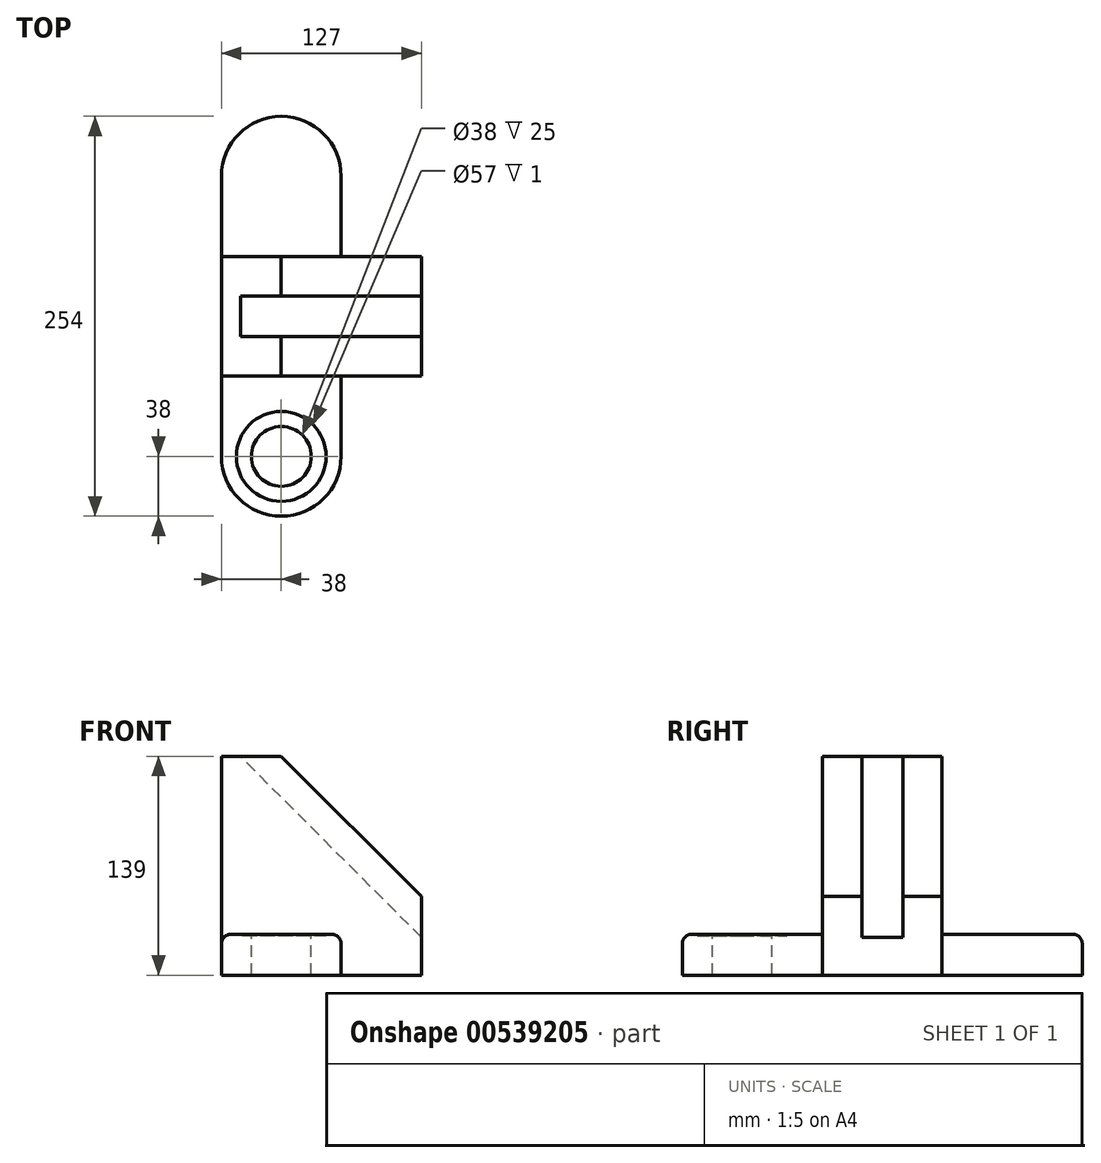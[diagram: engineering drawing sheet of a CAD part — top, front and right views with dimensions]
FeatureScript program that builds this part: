
annotation { "Feature Type Name" : "Feature", "Feature Type Description" : "" }
export const myFeature = defineFeature(function(context is Context, id is Id, definition is map)
    precondition{}
    {
        {
            assignVariable(context, id + "F0", {"name" : "b", "anyValue" : 38});
        }
        {
            var Q0;
            Q0=qCreatedBy(makeId("Top.planeOp"),FACE);
            var sketch = newSketch(context, id + "F1", { "sketchPlane" : qUnion([Q0])});
            skLineSegment(sketch, "E0.bottom", {"start": v(0, 0) * mm, "end": v(127, 0) * mm});
            skLineSegment(sketch, "E0.top", {"start": v(0, -76) * mm, "end": v(127, -76) * mm});
            skLineSegment(sketch, "E0.left", {"start": v(0, 0) * mm, "end": v(0, -76) * mm});
            skLineSegment(sketch, "E0.right", {"start": v(127, 0) * mm, "end": v(127, -76) * mm});
            skSolve(sketch);
        }
        {
            var Q0;
            Q0 = qSketchRegion(id + "F1", true);
            extrude(context, id + "F2", {"entities" : qUnion([Q0]), "depth" : (127 - getVariable(context, 'b') + 50) * mm, "offsetDistance" : 25 * mm});
        }
        {
            var Q0;
            Q0=makeQuery(id+"F2.opExtrude","CAP_FACE",FACE,{"disambiguationData":[OSD([sQuery(id+"F1.wireOp",EDGE,"E0.bottom"),sQuery(id+"F1.wireOp",EDGE,"E0.top"),sQuery(id+"F1.wireOp",EDGE,"E0.left"),sQuery(id+"F1.wireOp",EDGE,"E0.right")])],"isStart":true});
            var sketch = newSketch(context, id + "F3", { "sketchPlane" : qUnion([Q0])});
            skLineSegment(sketch, "E1", {"start": v(0, 127) * mm, "end": v(0, -51) * mm});
            skLineSegment(sketch, "E2", {"start": v(76, 127) * mm, "end": v(76, -51) * mm});
            skArc(sketch, "E3", {"start": v(0, 127) * mm, "mid": v(38, 165) * mm, "end": v(76, 127) * mm});
            skArc(sketch, "E4", {"start": v(0, -51) * mm, "mid": v(38, -89) * mm, "end": v(76, -51) * mm});
            skSolve(sketch);
        }
        {
            var Q0;
            Q0 = qSketchRegion(id + "F3", true);
            extrude(context, id + "F4", {"entities" : qUnion([Q0]), "operationType" : NewBodyOperationType.ADD, "oppositeDirection" : true, "depth" : 26 * mm, "offsetDistance" : 25 * mm});
        }
        {
            var Q0;
            {var subQ0=sQuery(id+"F3.wireOp",EDGE,"E2");var subQ1=sQuery(id+"F3.wireOp",EDGE,"E1");var subQ2=sQuery(id+"F3.wireOp",EDGE,"E3");Q0=makeQuery(id+"F4.boolean.opBoolean","SPLIT",FACE,{"disambiguationData":[TD([makeQuery(id+"F2.opExtrude","SWEPT_FACE",FACE,{"disambiguationData":[OSD([sQuery(id+"F1.wireOp",EDGE,"E0.top")])]})])],"derivedFrom":makeQuery(id+"F4.opExtrude","CAP_FACE",FACE,{"disambiguationData":[OSD([subQ1,subQ0,subQ2,sQuery(id+"F3.wireOp",EDGE,"E4")])],"isStart":false})});}
            var sketch = newSketch(context, id + "F5", { "sketchPlane" : qUnion([Q0])});
            skCircle(sketch, "E5", {"center": v(38, -127) * mm, "radius": 19 * mm});
            skSolve(sketch);
        }
        {
            var Q0;
            Q0 = qSketchRegion(id + "F5", true);
            extrude(context, id + "F6", {"entities" : qUnion([Q0]), "operationType" : NewBodyOperationType.REMOVE, "endBound" : BoundingType.UP_TO_NEXT, "oppositeDirection" : true, "depth" : 25 * mm, "offsetDistance" : 25 * mm});
        }
        {
            var Q0;
            {var subQ0=sQuery(id+"F3.wireOp",EDGE,"E2");var subQ1=sQuery(id+"F3.wireOp",EDGE,"E1");var subQ2=sQuery(id+"F3.wireOp",EDGE,"E3");Q0=makeQuery(id+"F4.boolean.opBoolean","SPLIT",FACE,{"disambiguationData":[TD([makeQuery(id+"F2.opExtrude","SWEPT_FACE",FACE,{"disambiguationData":[OSD([sQuery(id+"F1.wireOp",EDGE,"E0.top")])]})])],"derivedFrom":makeQuery(id+"F4.opExtrude","CAP_FACE",FACE,{"disambiguationData":[OSD([subQ1,subQ0,subQ2,sQuery(id+"F3.wireOp",EDGE,"E4")])],"isStart":false})});}
            var sketch = newSketch(context, id + "F7", { "sketchPlane" : qUnion([Q0])});
            skCircle(sketch, "E6", {"center": v(38, -127) * mm, "radius": 28.5 * mm});
            skSolve(sketch);
        }
        {
            var Q0;
            Q0 = qSketchRegion(id + "F7", true);
            extrude(context, id + "F8", {"entities" : qUnion([Q0]), "operationType" : NewBodyOperationType.REMOVE, "oppositeDirection" : true, "depth" : 1 * mm, "offsetDistance" : 25 * mm});
        }
        {
            var Q0;
            Q0=makeQuery(id+"F2.opExtrude","SWEPT_FACE",FACE,{"disambiguationData":[OSD([sQuery(id+"F1.wireOp",EDGE,"E0.top")])]});
            var Q1;
            Q1=makeQuery(id+"F2.opExtrude","SWEPT_FACE",FACE,{"disambiguationData":[OSD([sQuery(id+"F1.wireOp",EDGE,"E0.bottom")])]});
            cPlane(context, id + "F9", {"entities" : qUnion([Q0, Q1]), "cplaneType" : CPlaneType.MID_PLANE, "offset" : 25 * mm, "width" : 150 * mm, "height" : 150 * mm});
        }
        {
            var Q0;
            {var subQ1=sQuery(id+"F3.wireOp",EDGE,"E2");Q0=makeQuery(id+"F4.boolean.opBoolean","SPLIT",EDGE,{"disambiguationData":[TD([makeQuery(id+"F2.opExtrude","SWEPT_FACE",FACE,{"disambiguationData":[OSD([sQuery(id+"F1.wireOp",EDGE,"E0.top")])]})])],"derivedFrom":makeQuery(id+"F4.opExtrude","CAP_EDGE",EDGE,{"disambiguationData":[OSD([subQ1])],"isStart":false})});}
            var Q1;
            {var subQ1=sQuery(id+"F3.wireOp",EDGE,"E2");Q1=makeQuery(id+"F4.boolean.opBoolean","SPLIT",EDGE,{"disambiguationData":[TD([makeQuery(id+"F2.opExtrude","SWEPT_FACE",FACE,{"disambiguationData":[OSD([sQuery(id+"F1.wireOp",EDGE,"E0.bottom")])]})])],"derivedFrom":makeQuery(id+"F4.opExtrude","CAP_EDGE",EDGE,{"disambiguationData":[OSD([subQ1])],"isStart":false})});}
            fillet(context, id + "F10", {"entities" : qUnion([Q0, Q1]), "radius" : 6 * mm, "tangentPropagation" : true, "allowEdgeOverflow" : false});
        }
        {
            var Q0;
            Q0=makeQuery(id+"F2.opExtrude","SWEPT_FACE",FACE,{"disambiguationData":[OSD([sQuery(id+"F1.wireOp",EDGE,"E0.right")])]});
            var sketch = newSketch(context, id + "F11", { "sketchPlane" : qUnion([Q0])});
            skLineSegment(sketch, "E7", {"start": v(-76, 50) * mm, "end": v(0, 50) * mm});
            skSolve(sketch);
        }
        {
            var Q0;
            Q0=makeQuery(id+"F2.opExtrude","CAP_FACE",FACE,{"disambiguationData":[OSD([sQuery(id+"F1.wireOp",EDGE,"E0.bottom"),sQuery(id+"F1.wireOp",EDGE,"E0.top"),sQuery(id+"F1.wireOp",EDGE,"E0.left"),sQuery(id+"F1.wireOp",EDGE,"E0.right")])],"isStart":false});
            var sketch = newSketch(context, id + "F12", { "sketchPlane" : qUnion([Q0])});
            skLineSegment(sketch, "E8", {"start": v(38, -76) * mm, "end": v(38, 0) * mm});
            skSolve(sketch);
        }
        {
            var Q0;
            Q0=sQuery(id+"F11.wireOp",VERTEX,"E7.start");
            var Q1;
            Q1=sQuery(id+"F12.wireOp",VERTEX,"E8.start");
            var Q2;
            Q2=sQuery(id+"F12.wireOp",VERTEX,"E8.end");
            cPlane(context, id + "F13", {"entities" : qUnion([Q0, Q1, Q2]), "cplaneType" : CPlaneType.THREE_POINT, "offset" : 25 * mm, "width" : 150 * mm, "height" : 150 * mm});
        }
        {
            var Q0;
            {var subQ0=sQuery(id+"F11.wireOp",EDGE,"E7");Q0=makeQuery(id+"F11.imprint","IMPRINT",FACE,{"disambiguationData":[TD([[makeQuery(id+"F11.imprint","IMPRINT",EDGE,{"derivedFrom":subQ0}),1.0]])]});}
            var Q1;
            Q1=qCreatedBy(id+"F13.planeOp",FACE);
            extrude(context, id + "F14", {"entities" : qUnion([Q0]), "operationType" : NewBodyOperationType.REMOVE, "endBound" : BoundingType.UP_TO_SURFACE, "oppositeDirection" : true, "depth" : 25 * mm, "endBoundEntityFace" : qUnion([Q1]), "offsetDistance" : 25 * mm});
        }
        {
            var Q0;
            {var subQ0=sQuery(id+"F12.wireOp",EDGE,"E8");Q0=makeQuery(id+"F12.imprint","IMPRINT",FACE,{"disambiguationData":[TD([[makeQuery(id+"F12.imprint","IMPRINT",EDGE,{"derivedFrom":subQ0}),1.0]])]});}
            var sketch = newSketch(context, id + "F15", { "sketchPlane" : qUnion([Q0])});
            skLineSegment(sketch, "E9", {"start": v(12, -76) * mm, "end": v(12, 0) * mm});
            skSolve(sketch);
        }
        {
            var Q0;
            Q0=sQuery(id+"F15.wireOp",EDGE,"E9");
            cPlane(context, id + "F16", {"entities" : qUnion([Q0]), "cplaneType" : CPlaneType.LINE_ANGLE, "offset" : 25 * mm, "angle" : 45 * degree, "width" : 150 * mm, "height" : 150 * mm});
        }
        {
            var Q0;
            {var subQ0=sQuery(id+"F12.wireOp",EDGE,"E8");Q0=makeQuery(id+"F12.imprint","IMPRINT",FACE,{"disambiguationData":[TD([[makeQuery(id+"F12.imprint","IMPRINT",EDGE,{"derivedFrom":subQ0}),1.0]])]});}
            var sketch = newSketch(context, id + "F17", { "sketchPlane" : qUnion([Q0])});
            skLineSegment(sketch, "E10.bottom", {"start": v(38, -25) * mm, "end": v(12, -25) * mm});
            skLineSegment(sketch, "E10.top", {"start": v(38, -51) * mm, "end": v(12, -51) * mm});
            skLineSegment(sketch, "E10.left", {"start": v(38, -25) * mm, "end": v(38, -51) * mm});
            skLineSegment(sketch, "E10.right", {"start": v(12, -25) * mm, "end": v(12, -51) * mm});
            skSolve(sketch);
        }
        {
            var Q0;
            Q0=makeQuery(id+"F14.boolean.opBoolean","COPY",FACE,{"derivedFrom":makeQuery(id+"F14.opExtrude","CAP_FACE",FACE,{"disambiguationData":[OSD([sQuery(id+"F1.wireOp",EDGE,"E0.bottom"),sQuery(id+"F1.wireOp",EDGE,"E0.top"),sQuery(id+"F1.wireOp",EDGE,"E0.right"),sQuery(id+"F11.wireOp",EDGE,"E7")])],"isStart":false})});
            var sketch = newSketch(context, id + "F18", { "sketchPlane" : qUnion([Q0])});
            skLineSegment(sketch, "E11.bottom", {"start": v(-51, 71.42) * mm, "end": v(-25, 71.42) * mm});
            skLineSegment(sketch, "E11.top", {"start": v(-51, -54.45) * mm, "end": v(-25, -54.45) * mm});
            skLineSegment(sketch, "E11.left", {"start": v(-51, 71.42) * mm, "end": v(-51, -54.45) * mm});
            skLineSegment(sketch, "E11.right", {"start": v(-25, 71.42) * mm, "end": v(-25, -54.45) * mm});
            skSolve(sketch);
        }
        {
            var Q0;
            Q0=makeQuery(id+"F2.opExtrude","SWEPT_FACE",FACE,{"disambiguationData":[OSD([sQuery(id+"F1.wireOp",EDGE,"E0.right")])]});
            var sketch = newSketch(context, id + "F19", { "sketchPlane" : qUnion([Q0])});
            skLineSegment(sketch, "E12.bottom", {"start": v(-51, 50) * mm, "end": v(-25, 50) * mm});
            skLineSegment(sketch, "E12.top", {"start": v(-51, 24) * mm, "end": v(-25, 24) * mm});
            skLineSegment(sketch, "E12.left", {"start": v(-51, 50) * mm, "end": v(-51, 24) * mm});
            skLineSegment(sketch, "E12.right", {"start": v(-25, 50) * mm, "end": v(-25, 24) * mm});
            skSolve(sketch);
        }
        {
            var Q0;
            Q0=makeQuery(id+"F18.imprint","IMPRINT",FACE,{"disambiguationData":[TD([[makeQuery(id+"F18.imprint","IMPRINT",EDGE,{"derivedFrom":sQuery(id+"F18.wireOp",EDGE,"E11.bottom")}),-1.0]])]});
            var Q1;
            Q1=makeQuery(id+"F17.imprint","IMPRINT",FACE,{"disambiguationData":[TD([[makeQuery(id+"F17.imprint","IMPRINT",EDGE,{"derivedFrom":sQuery(id+"F17.wireOp",EDGE,"E10.bottom")}),1.0]])]});
            var Q2;
            Q2=makeQuery(id+"F19.imprint","IMPRINT",FACE,{"disambiguationData":[TD([[makeQuery(id+"F19.imprint","IMPRINT",EDGE,{"derivedFrom":sQuery(id+"F19.wireOp",EDGE,"E12.bottom")}),-1.0]])]});
            var Q3;
            Q3=qCreatedBy(id+"F16.planeOp",FACE);
            extrude(context, id + "F20", {"entities" : qUnion([Q0, Q1, Q2]), "operationType" : NewBodyOperationType.REMOVE, "endBound" : BoundingType.UP_TO_SURFACE, "oppositeDirection" : true, "depth" : 25 * mm, "endBoundEntityFace" : qUnion([Q3]), "offsetDistance" : 25 * mm});
        }
    });
